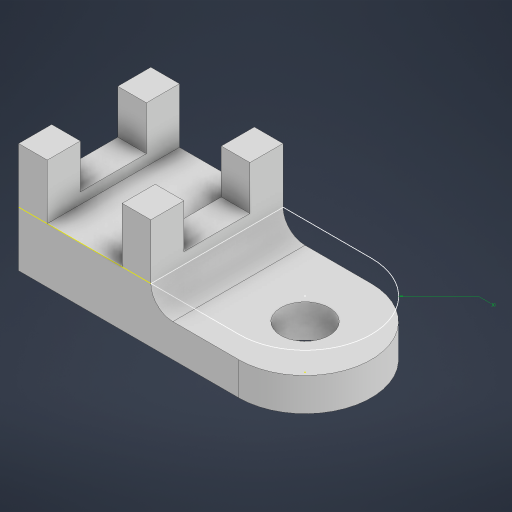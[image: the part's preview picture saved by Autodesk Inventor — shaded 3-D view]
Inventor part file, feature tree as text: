
AUTODESK INVENTOR PART (.ipt)
format: ipt  version: 2023 (Build 270158000, 158)  size: 251,392 bytes
history: native  units: mm
features: sketch x7, extrude x5, other x2, hole x1
ambient origin geometry x8: Origin, YZ Plane, XZ Plane, XY Plane, X Axis, Y Axis, Z Axis, Center Point
bodies: Body1 (feature_tree)
feature tree (15):
  other  "Bryła1"
  extrude  "Wyciągnięcie proste1"  Depth=130.0mm
  hole  "Otwór1"  [1 undecoded]
  extrude  "Wyciągnięcie proste2"  Depth=30.0mm
  extrude  "Wyciągnięcie proste3"  Depth=25.0mm TaperAngle=0.0deg
  extrude  "Wyciągnięcie proste4"  Depth=60.0mm
  sketch  "Szkic6"
  sketch  "Szkic7"
  extrude  "Wyciągnięcie proste5"  Depth=60.0mm
  other  "Zaokrąglenie powierzchni1"
  sketch  "Szkic1"
  sketch  "Szkic2"
  sketch  "Szkic3"
  sketch  "Szkic4"
  sketch  "Szkic5"
note: 1 required parameter value undecoded (feature->parameter linkage not recoverable at this tier; creation-order binding heuristic only, values carry confidence <= 0.55)
